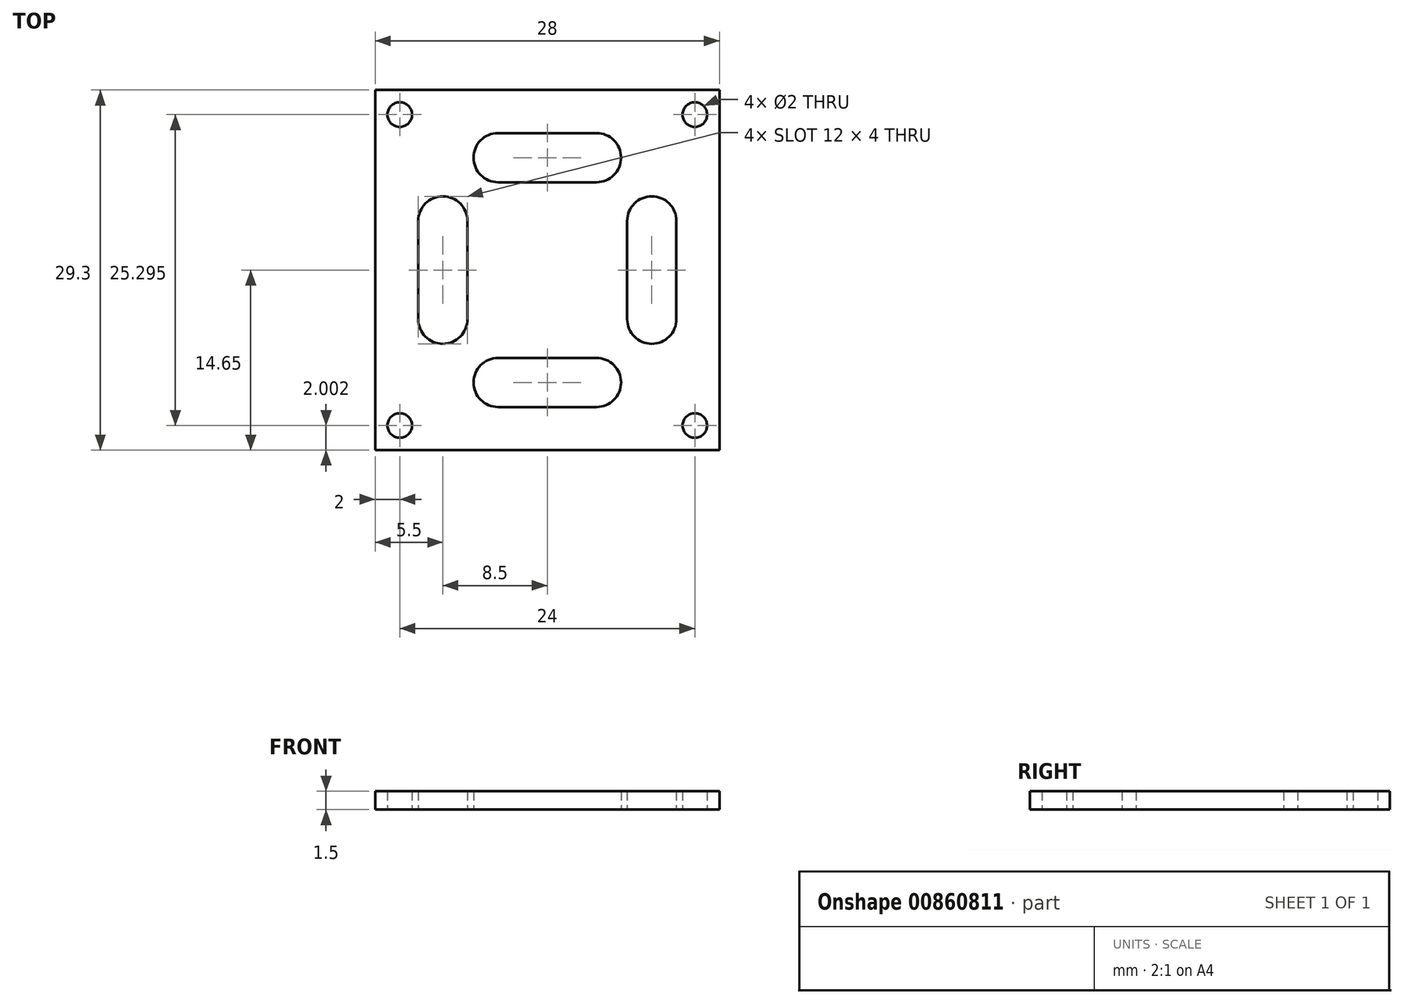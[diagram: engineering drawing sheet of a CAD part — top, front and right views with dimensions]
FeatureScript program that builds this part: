
annotation { "Feature Type Name" : "Feature", "Feature Type Description" : "" }
export const myFeature = defineFeature(function(context is Context, id is Id, definition is map)
    precondition{}
    {
        {
            var Q0;
            Q0=qCreatedBy(makeId("Top.planeOp"),FACE);
            var sketch = newSketch(context, id + "F0", { "sketchPlane" : qUnion([Q0])});
            skLineSegment(sketch, "E0", {"start": v(-4, 11.15) * mm, "end": v(4, 11.15) * mm});
            skArc(sketch, "E1", {"start": v(4, 11.15) * mm, "mid": v(5.41, 10.56) * mm, "end": v(6, 9.15) * mm});
            skArc(sketch, "E2", {"start": v(6, 9.15) * mm, "mid": v(5.41, 7.73) * mm, "end": v(4, 7.15) * mm});
            skLineSegment(sketch, "E3", {"start": v(4, 7.15) * mm, "end": v(-4, 7.15) * mm});
            skArc(sketch, "E4", {"start": v(-4, 7.15) * mm, "mid": v(-5.41, 7.73) * mm, "end": v(-6, 9.15) * mm});
            skArc(sketch, "E5", {"start": v(-6, 9.15) * mm, "mid": v(-5.41, 10.56) * mm, "end": v(-4, 11.15) * mm});
            skLineSegment(sketch, "E6", {"start": v(-14, 14.65) * mm, "end": v(14, 14.65) * mm});
            skLineSegment(sketch, "E7", {"start": v(14, 14.65) * mm, "end": v(14, -14.65) * mm});
            skLineSegment(sketch, "E8", {"start": v(14, -14.65) * mm, "end": v(-14, -14.65) * mm});
            skLineSegment(sketch, "E9", {"start": v(-14, -14.65) * mm, "end": v(-14, 14.65) * mm});
            skArc(sketch, "E10", {"start": v(-8.5, 6) * mm, "mid": v(-7.09, 5.41) * mm, "end": v(-6.5, 4) * mm});
            skLineSegment(sketch, "E11", {"start": v(-6.5, 4) * mm, "end": v(-6.5, -4) * mm});
            skArc(sketch, "E12", {"start": v(-6.5, -4) * mm, "mid": v(-7.09, -5.41) * mm, "end": v(-8.5, -6) * mm});
            skArc(sketch, "E13", {"start": v(-8.5, -6) * mm, "mid": v(-9.91, -5.41) * mm, "end": v(-10.5, -4) * mm});
            skLineSegment(sketch, "E14", {"start": v(-10.5, -4) * mm, "end": v(-10.5, 4) * mm});
            skArc(sketch, "E15", {"start": v(-10.5, 4) * mm, "mid": v(-9.91, 5.41) * mm, "end": v(-8.5, 6) * mm});
            skArc(sketch, "E16", {"start": v(8.5, 6) * mm, "mid": v(7.09, 5.41) * mm, "end": v(6.5, 4) * mm});
            skLineSegment(sketch, "E17", {"start": v(6.5, 4) * mm, "end": v(6.5, -4) * mm});
            skArc(sketch, "E18", {"start": v(6.5, -4) * mm, "mid": v(7.09, -5.41) * mm, "end": v(8.5, -6) * mm});
            skArc(sketch, "E19", {"start": v(8.5, -6) * mm, "mid": v(9.91, -5.41) * mm, "end": v(10.5, -4) * mm});
            skLineSegment(sketch, "E20", {"start": v(10.5, -4) * mm, "end": v(10.5, 4) * mm});
            skArc(sketch, "E21", {"start": v(10.5, 4) * mm, "mid": v(9.91, 5.41) * mm, "end": v(8.5, 6) * mm});
            skLineSegment(sketch, "E22", {"start": v(-4, -11.15) * mm, "end": v(4, -11.15) * mm});
            skArc(sketch, "E23", {"start": v(4, -11.15) * mm, "mid": v(5.41, -10.56) * mm, "end": v(6, -9.15) * mm});
            skArc(sketch, "E24", {"start": v(6, -9.15) * mm, "mid": v(5.41, -7.73) * mm, "end": v(4, -7.15) * mm});
            skLineSegment(sketch, "E25", {"start": v(4, -7.15) * mm, "end": v(-4, -7.15) * mm});
            skArc(sketch, "E26", {"start": v(-4, -7.15) * mm, "mid": v(-5.41, -7.73) * mm, "end": v(-6, -9.15) * mm});
            skArc(sketch, "E27", {"start": v(-6, -9.15) * mm, "mid": v(-5.41, -10.56) * mm, "end": v(-4, -11.15) * mm});
            skCircle(sketch, "E28", {"center": v(-12, 12.65) * mm, "radius": 1 * mm});
            skCircle(sketch, "E29", {"center": v(12, 12.65) * mm, "radius": 1 * mm});
            skCircle(sketch, "E30", {"center": v(12, -12.65) * mm, "radius": 1 * mm});
            skCircle(sketch, "E31", {"center": v(-12, -12.65) * mm, "radius": 1 * mm});
            skSolve(sketch);
        }
        {
            var Q0;
            Q0 = qSketchRegion(id + "F0", true);
            extrude(context, id + "F1", {"entities" : qUnion([Q0]), "depth" : 1.5 * mm, "offsetDistance" : 25 * mm});
        }
    });
